# Revit family: WC MURANO_RFA
name_source: partatom
category: Aparatos sanitarios
units: mm (PartAtom-declared; Revit-internal decimal feet)

## family parameters
Compartido = Sí
Corte con vacíos al cargar = No
Cota de conector redondo = Diámetro de uso
Número OmniClass = 23.45.00.00
Punto de cálculo de habitación = No
Se basa en plano de trabajo = Sí
Siempre vertical = Sí
Tipo de pieza = Normal
Título OmniClass = Sanitary, Laundry, and Cleaning Equipment

## types (1)
- WC MURANO
    Accessories = Tapa de cierre lento con sistema de fijación. Reducción para válvula de admisión deØ15/16-14 NS-1 a 1/2-14 NPSM
    Características del Producto = Diseño ergonómico de construcción robusta con cerámica de 10mm de espesor, con sistema de descarga tipo vórtice con sifón jet y espejo de agua óptimo, mueblelibre de alabeo (base plana).
    Comentarios de tipo = WC Murano
    Conexión de Alimentación = A la alimentacion Ø15/16-14 NS-1
    Conexión de Descarga = A la descarga se acopla al Ø de drenaje de 4" con brida sanitaria o cuello de cera.
    Descripción = WC con Trampa Oculta, una Descarga de 4.8 l, con Asiento de Cierre Lento
    Elevación por defecto = 0.0"
    Fabricante = Helvex S.A. de C.V.
    Materials = Cerámica porcelanizada de alto brillo Grado de Calidad "A", Tipo I Trampa oculta
    Maximum Consumption = 4,8 lpd
    Modelo = WC MURANO
    Operation = Sistema de una descarga
    Presión Máxima de Trabajo = 85.3 psi
    Presión Mínima de Trabajo = 3.6 psi
    URL = https://helvex.com.mx
    Valves = Valv. de admisión y descarga certificadas, Valv. de admisión silenciosa, válvulas armadas y calibradas, válvula de descarga con sello hermético

## geometry (parser evidence)
native form markers: Sweep x3
no freeform markers — native parametric forms only
